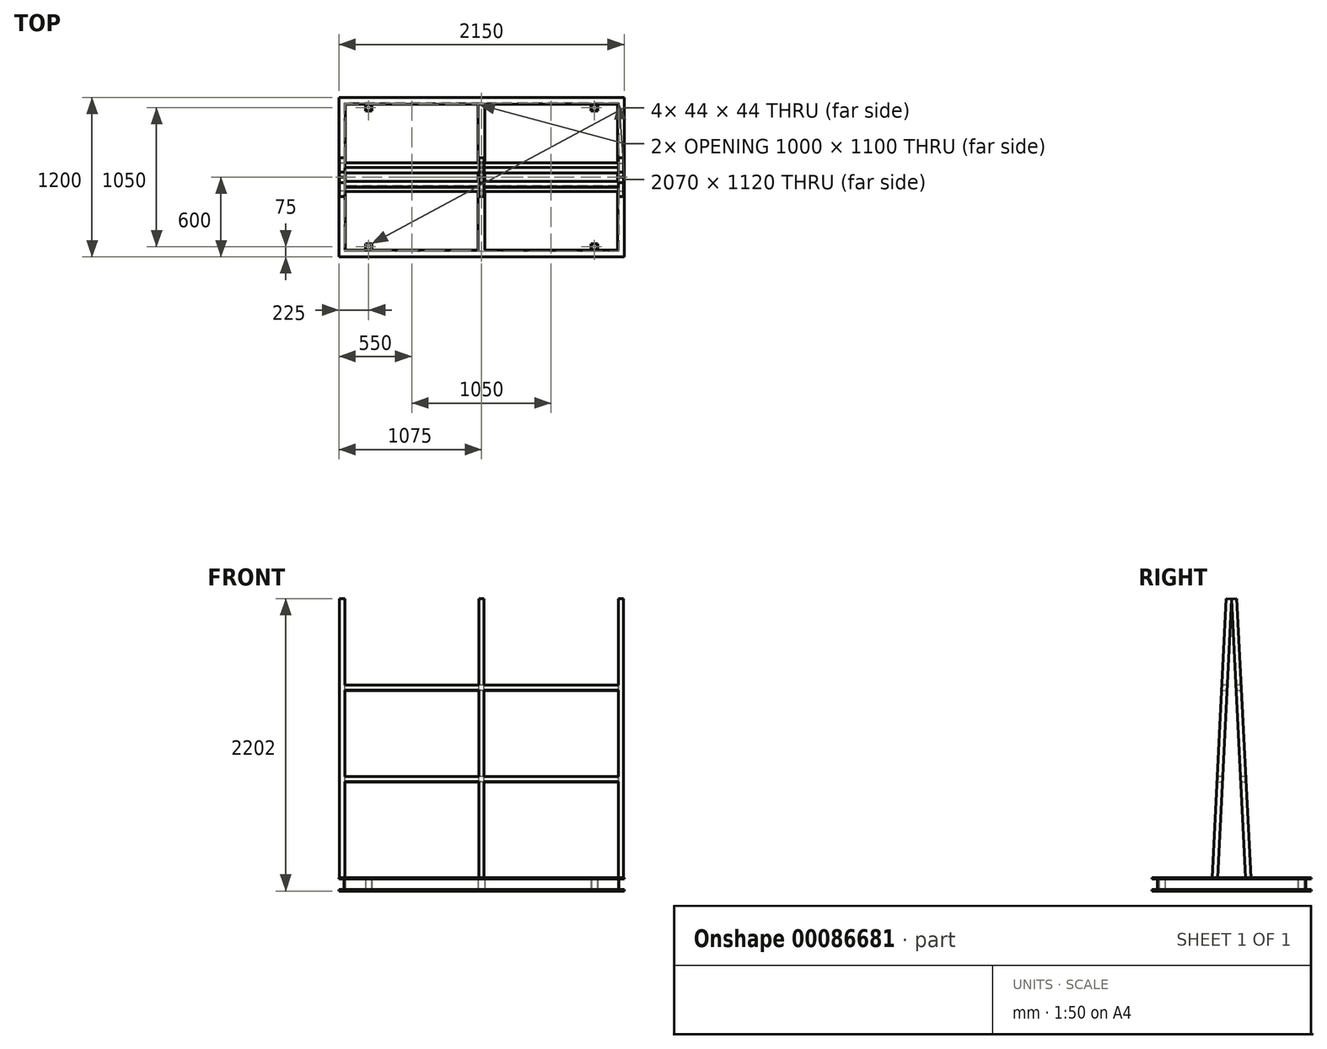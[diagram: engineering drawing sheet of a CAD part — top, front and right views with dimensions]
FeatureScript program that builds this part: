
annotation { "Feature Type Name" : "Feature", "Feature Type Description" : "" }
export const myFeature = defineFeature(function(context is Context, id is Id, definition is map)
    precondition{}
    {
        {
            var Q0;
            Q0=qCreatedBy(makeId("Top.planeOp"),FACE);
            var sketch = newSketch(context, id + "F0", { "sketchPlane" : qUnion([Q0])});
            skLineSegment(sketch, "E0.rect.bottom", {"start": v(1075, 600) * mm, "end": v(-1075, 600) * mm});
            skLineSegment(sketch, "E0.rect.top", {"start": v(1075, -600) * mm, "end": v(-1075, -600) * mm});
            skLineSegment(sketch, "E0.rect.left", {"start": v(1075, 600) * mm, "end": v(1075, -600) * mm});
            skLineSegment(sketch, "E0.rect.right", {"start": v(-1075, 600) * mm, "end": v(-1075, -600) * mm});
            skPoint(sketch, "E0.rect.middle", {"position": v(0, 0) * mm});
            skLineSegment(sketch, "E1.rect.bottom", {"start": v(1025, 550) * mm, "end": v(25, 550) * mm});
            skLineSegment(sketch, "E1.rect.top", {"start": v(1025, -550) * mm, "end": v(25, -550) * mm});
            skLineSegment(sketch, "E1.rect.left", {"start": v(1025, 550) * mm, "end": v(1025, -550) * mm});
            skLineSegment(sketch, "E1.rect.right", {"start": v(-1025, 550) * mm, "end": v(-1025, -550) * mm});
            skLineSegment(sketch, "E2.rect.left", {"start": v(25, 550) * mm, "end": v(25, -550) * mm});
            skLineSegment(sketch, "E2.rect.right", {"start": v(-25, 550) * mm, "end": v(-25, -550) * mm});
            skLineSegment(sketch, "E3.trimOffspring", {"start": v(-25, 550) * mm, "end": v(-1025, 550) * mm});
            skLineSegment(sketch, "E4.trimOffspring", {"start": v(-25, -550) * mm, "end": v(-1025, -550) * mm});
            skSolve(sketch);
        }
        {
            var Q0;
            Q0=makeQuery(id+"F0.imprint","IMPRINT",FACE,{"disambiguationData":[TD([[makeQuery(id+"F0.imprint","IMPRINT",EDGE,{"derivedFrom":sQuery(id+"F0.wireOp",EDGE,"E0.rect.bottom")}),1.0]])]});
            extrude(context, id + "F1", {"entities" : qUnion([Q0]), "depth" : 100 * mm});
        }
        {
            var Q0;
            Q0=makeQuery(id+"F1.opExtrude","SWEPT_FACE",FACE,{"disambiguationData":[OSD([sQuery(id+"F0.wireOp",EDGE,"E0.rect.right")])]});
            var sketch = newSketch(context, id + "F2", { "sketchPlane" : qUnion([Q0])});
            skLineSegment(sketch, "E5.bottom", {"start": v(-600, 90) * mm, "end": v(-560, 90) * mm});
            skLineSegment(sketch, "E5.top", {"start": v(-600, 10) * mm, "end": v(-560, 10) * mm});
            skLineSegment(sketch, "E5.left", {"start": v(-600, 90) * mm, "end": v(-600, 10) * mm});
            skLineSegment(sketch, "E5.right", {"start": v(-560, 90) * mm, "end": v(-560, 10) * mm});
            skLineSegment(sketch, "E6.bottom", {"start": v(600, 90) * mm, "end": v(560, 90) * mm});
            skLineSegment(sketch, "E6.top", {"start": v(600, 10) * mm, "end": v(560, 10) * mm});
            skLineSegment(sketch, "E6.left", {"start": v(600, 90) * mm, "end": v(600, 10) * mm});
            skLineSegment(sketch, "E6.right", {"start": v(560, 90) * mm, "end": v(560, 10) * mm});
            skSolve(sketch);
        }
        {
            var Q0;
            Q0=makeQuery(id+"F2.imprint","IMPRINT",FACE,{"disambiguationData":[TD([[makeQuery(id+"F2.imprint","IMPRINT",EDGE,{"derivedFrom":sQuery(id+"F2.wireOp",EDGE,"E5.bottom")}),-1.0]])]});
            var Q1;
            Q1=makeQuery(id+"F2.imprint","IMPRINT",FACE,{"disambiguationData":[TD([[makeQuery(id+"F2.imprint","IMPRINT",EDGE,{"derivedFrom":sQuery(id+"F2.wireOp",EDGE,"E6.bottom")}),1.0]])]});
            extrude(context, id + "F3", {"entities" : qUnion([Q0, Q1]), "operationType" : NewBodyOperationType.REMOVE, "endBound" : BoundingType.THROUGH_ALL, "oppositeDirection" : true, "depth" : 25 * mm});
        }
        {
            var Q0;
            Q0=makeQuery(id+"F3.boolean.opBoolean","COPY",FACE,{"derivedFrom":makeQuery(id+"F3.opExtrude","SWEPT_FACE",FACE,{"disambiguationData":[OSD([sQuery(id+"F2.wireOp",EDGE,"E6.right")])]})});
            var sketch = newSketch(context, id + "F4", { "sketchPlane" : qUnion([Q0])});
            skLineSegment(sketch, "E7.bottom", {"start": v(1075, 90) * mm, "end": v(1035, 90) * mm});
            skLineSegment(sketch, "E7.top", {"start": v(1075, 10) * mm, "end": v(1035, 10) * mm});
            skLineSegment(sketch, "E7.left", {"start": v(1075, 90) * mm, "end": v(1075, 10) * mm});
            skLineSegment(sketch, "E7.right", {"start": v(1035, 90) * mm, "end": v(1035, 10) * mm});
            skLineSegment(sketch, "E8.bottom", {"start": v(-1075, 90) * mm, "end": v(-1035, 90) * mm});
            skLineSegment(sketch, "E8.top", {"start": v(-1075, 10) * mm, "end": v(-1035, 10) * mm});
            skLineSegment(sketch, "E8.left", {"start": v(-1075, 90) * mm, "end": v(-1075, 10) * mm});
            skLineSegment(sketch, "E8.right", {"start": v(-1035, 90) * mm, "end": v(-1035, 10) * mm});
            skSolve(sketch);
        }
        {
            var Q0;
            Q0=makeQuery(id+"F4.imprint","IMPRINT",FACE,{"disambiguationData":[TD([[makeQuery(id+"F4.imprint","IMPRINT",EDGE,{"derivedFrom":sQuery(id+"F4.wireOp",EDGE,"E7.bottom")}),1.0]])]});
            var Q1;
            Q1=makeQuery(id+"F4.imprint","IMPRINT",FACE,{"disambiguationData":[TD([[makeQuery(id+"F4.imprint","IMPRINT",EDGE,{"derivedFrom":sQuery(id+"F4.wireOp",EDGE,"E8.bottom")}),1.0]])]});
            extrude(context, id + "F5", {"entities" : qUnion([Q0, Q1]), "operationType" : NewBodyOperationType.REMOVE, "endBound" : BoundingType.THROUGH_ALL, "oppositeDirection" : true, "depth" : 25 * mm});
        }
        {
            var Q0;
            Q0=qCreatedBy(makeId("Front.planeOp"),FACE);
            var sketch = newSketch(context, id + "F6", { "sketchPlane" : qUnion([Q0])});
            skLineSegment(sketch, "E9.bottom", {"start": v(0, 10) * mm, "end": v(-90, 10) * mm});
            skLineSegment(sketch, "E9.top", {"start": v(0, 90) * mm, "end": v(-90, 90) * mm});
            skLineSegment(sketch, "E9.left", {"start": v(0, 10) * mm, "end": v(0, 90) * mm});
            skLineSegment(sketch, "E9.right", {"start": v(-90, 10) * mm, "end": v(-90, 90) * mm});
            skSolve(sketch);
        }
        {
            var Q0;
            Q0=qSketchRegion(id+"F6",true);
            var Q1;
            Q1=makeQuery(id+"F1.opExtrude","SWEPT_FACE",FACE,{"disambiguationData":[OSD([sQuery(id+"F0.wireOp",EDGE,"E3.trimOffspring")])]});
            var Q2;
            Q2=makeQuery(id+"F1.opExtrude","SWEPT_FACE",FACE,{"disambiguationData":[OSD([sQuery(id+"F0.wireOp",EDGE,"E4.trimOffspring")])]});
            extrude(context, id + "F7", {"entities" : qUnion([Q0]), "operationType" : NewBodyOperationType.REMOVE, "endBound" : BoundingType.UP_TO_SURFACE, "oppositeDirection" : true, "endBoundEntityFace" : qUnion([Q1]), "depth" : 25 * mm, "hasSecondDirection" : true, "secondDirectionBound" : SecondDirectionBoundingType.UP_TO_SURFACE, "secondDirectionOppositeDirection" : false, "secondDirectionBoundEntityFace" : qUnion([Q2]), "secondDirectionDepth" : 25 * mm});
        }
        {
            var Q0;
            Q0=qCreatedBy(makeId("Right.planeOp"),FACE);
            cPlane(context, id + "F8", {"entities" : qUnion([Q0]), "cplaneType" : CPlaneType.OFFSET, "offset" : 525 * mm, "width" : 150 * mm, "height" : 150 * mm});
        }
        {
            var Q0;
            Q0=qCreatedBy(makeId("Right.planeOp"),FACE);
            var sketch = newSketch(context, id + "F9", { "sketchPlane" : qUnion([Q0])});
            skLineSegment(sketch, "E10", {"start": v(144.95, 100) * mm, "end": v(-249.42, 100) * mm});
            skLineSegment(sketch, "E11", {"start": v(0, 0) * mm, "end": v(185.49, 0) * mm});
            skLineSegment(sketch, "E12", {"start": v(104.9, 100) * mm, "end": v(-0.05, 2200) * mm});
            skLineSegment(sketch, "E13", {"start": v(-105, 100) * mm, "end": v(0, 2200) * mm});
            skLineSegment(sketch, "E14.0", {"start": v(144.95, 100) * mm, "end": v(39.9, 2202) * mm});
            skLineSegment(sketch, "E15.0", {"start": v(-145.05, 100) * mm, "end": v(-39.95, 2202) * mm});
            skLineSegment(sketch, "E16", {"start": v(-39.95, 2202) * mm, "end": v(0, 2200) * mm});
            skLineSegment(sketch, "E17", {"start": v(-0.05, 2200) * mm, "end": v(39.9, 2202) * mm});
            skLineSegment(sketch, "E18", {"start": v(0, 0) * mm, "end": v(0, 2304.84) * mm});
            skSolve(sketch);
        }
        {
            var Q0;
            {var subQ7=sQuery(id+"F9.wireOp",EDGE,"E15.0");Q0=makeQuery(id+"F9.imprint","IMPRINT",FACE,{"disambiguationData":[TD([[makeQuery(id+"F9.imprint","IMPRINT",EDGE,{"derivedFrom":subQ7}),-1.0]])]});}
            var Q1;
            {var subQ1=sQuery(id+"F9.wireOp",EDGE,"E14.0");Q1=makeQuery(id+"F9.imprint","IMPRINT",FACE,{"disambiguationData":[TD([[makeQuery(id+"F9.imprint","IMPRINT",EDGE,{"derivedFrom":subQ1}),1.0]])]});}
            extrude(context, id + "F10", {"entities" : qUnion([Q0, Q1]), "endBound" : BoundingType.SYMMETRIC, "depth" : 40 * mm});
        }
        {
            var Q0;
            Q0=makeQuery(id+"F10.opExtrude","SWEPT_BODY",BODY,{"disambiguationData":[OSD([sQuery(id+"F9.wireOp",EDGE,"E10"),sQuery(id+"F9.wireOp",EDGE,"E12"),sQuery(id+"F9.wireOp",EDGE,"E14.0"),sQuery(id+"F9.wireOp",EDGE,"E17"),sQuery(id+"F9.wireOp",EDGE,"E18")])]});
            var Q1;
            Q1=makeQuery(id+"F10.opExtrude","SWEPT_BODY",BODY,{"disambiguationData":[OSD([sQuery(id+"F9.wireOp",EDGE,"E10"),sQuery(id+"F9.wireOp",EDGE,"E12"),sQuery(id+"F9.wireOp",EDGE,"E13"),sQuery(id+"F9.wireOp",EDGE,"E15.0"),sQuery(id+"F9.wireOp",EDGE,"E16"),sQuery(id+"F9.wireOp",EDGE,"E17")])]});
            var Q2;
            Q2=qCreatedBy(id+"F8.planeOp",FACE);
            mirror(context, id + "F11", {"operationType" : NewBodyOperationType.ADD, "entities" : qUnion([Q0, Q1]), "mirrorPlane" : qUnion([Q2])});
        }
        {
            var Q0;
            Q0=makeQuery(id+"F1.opExtrude","SWEPT_BODY",BODY,{"disambiguationData":[OSD([sQuery(id+"F0.wireOp",EDGE,"E0.rect.bottom"),sQuery(id+"F0.wireOp",EDGE,"E0.rect.top"),sQuery(id+"F0.wireOp",EDGE,"E0.rect.left"),sQuery(id+"F0.wireOp",EDGE,"E0.rect.right"),sQuery(id+"F0.wireOp",EDGE,"E1.rect.bottom"),sQuery(id+"F0.wireOp",EDGE,"E1.rect.top"),sQuery(id+"F0.wireOp",EDGE,"E1.rect.left"),sQuery(id+"F0.wireOp",EDGE,"E1.rect.right"),sQuery(id+"F0.wireOp",EDGE,"E2.rect.left"),sQuery(id+"F0.wireOp",EDGE,"E2.rect.right"),sQuery(id+"F0.wireOp",EDGE,"E3.trimOffspring"),sQuery(id+"F0.wireOp",EDGE,"E4.trimOffspring")])]});
            var Q1;
            Q1=makeQuery(id+"F1.opExtrude","SWEPT_BODY",BODY,{"disambiguationData":[OSD([sQuery(id+"F0.wireOp",EDGE,"E0.rect.bottom"),sQuery(id+"F0.wireOp",EDGE,"E0.rect.top"),sQuery(id+"F0.wireOp",EDGE,"E0.rect.left"),sQuery(id+"F0.wireOp",EDGE,"E0.rect.right"),sQuery(id+"F0.wireOp",EDGE,"E1.rect.bottom"),sQuery(id+"F0.wireOp",EDGE,"E1.rect.top"),sQuery(id+"F0.wireOp",EDGE,"E1.rect.left"),sQuery(id+"F0.wireOp",EDGE,"E1.rect.right"),sQuery(id+"F0.wireOp",EDGE,"E2.rect.left"),sQuery(id+"F0.wireOp",EDGE,"E2.rect.right"),sQuery(id+"F0.wireOp",EDGE,"E3.trimOffspring"),sQuery(id+"F0.wireOp",EDGE,"E4.trimOffspring")])]});
            var Q2;
            Q2=qCreatedBy(makeId("Right.planeOp"),FACE);
            mirror(context, id + "F12", {"operationType" : NewBodyOperationType.ADD, "entities" : qUnion([Q0, Q1]), "mirrorPlane" : qUnion([Q2])});
        }
        {
            var Q0;
            Q0=makeQuery(id+"F12.opPattern","COPY",FACE,{"derivedFrom":makeQuery(id+"F11.opPattern","COPY",FACE,{"derivedFrom":makeQuery(id+"F10.opExtrude","CAP_FACE",FACE,{"disambiguationData":[OSD([sQuery(id+"F9.wireOp",EDGE,"E10"),sQuery(id+"F9.wireOp",EDGE,"E12"),sQuery(id+"F9.wireOp",EDGE,"E13"),sQuery(id+"F9.wireOp",EDGE,"E15.0"),sQuery(id+"F9.wireOp",EDGE,"E16"),sQuery(id+"F9.wireOp",EDGE,"E17")])],"isStart":false}),"instanceName":"1"}),"instanceName":"1"});
            var sketch = newSketch(context, id + "F13", { "sketchPlane" : qUnion([Q0])});
            skLineSegment(sketch, "E19", {"start": v(-72.4, 1552.8) * mm, "end": v(-32.46, 1550.81) * mm});
            skLineSegment(sketch, "E20", {"start": v(-32.46, 1550.81) * mm, "end": v(-34.46, 1510.86) * mm});
            skLineSegment(sketch, "E21", {"start": v(-34.46, 1510.86) * mm, "end": v(-74.4, 1512.86) * mm});
            skLineSegment(sketch, "E22", {"start": v(-74.4, 1512.86) * mm, "end": v(-72.4, 1552.8) * mm});
            skLineSegment(sketch, "E23", {"start": v(-106.87, 863.67) * mm, "end": v(-66.92, 861.67) * mm});
            skLineSegment(sketch, "E24", {"start": v(-66.92, 861.67) * mm, "end": v(-68.91, 821.72) * mm});
            skLineSegment(sketch, "E25", {"start": v(-68.91, 821.72) * mm, "end": v(-108.86, 823.72) * mm});
            skLineSegment(sketch, "E26", {"start": v(-108.86, 823.72) * mm, "end": v(-106.87, 863.67) * mm});
            skSolve(sketch);
        }
        {
            var Q0;
            Q0=makeQuery(id+"F13.imprint","IMPRINT",FACE,{"disambiguationData":[TD([[makeQuery(id+"F13.imprint","IMPRINT",EDGE,{"derivedFrom":sQuery(id+"F13.wireOp",EDGE,"E19")}),-1.0]])]});
            var Q1;
            Q1=makeQuery(id+"F13.imprint","IMPRINT",FACE,{"disambiguationData":[TD([[makeQuery(id+"F13.imprint","IMPRINT",EDGE,{"derivedFrom":sQuery(id+"F13.wireOp",EDGE,"E23")}),-1.0]])]});
            var Q2;
            Q2=makeQuery(id+"F11.opPattern","COPY",FACE,{"derivedFrom":makeQuery(id+"F10.opExtrude","CAP_FACE",FACE,{"disambiguationData":[OSD([sQuery(id+"F9.wireOp",EDGE,"E10"),sQuery(id+"F9.wireOp",EDGE,"E12"),sQuery(id+"F9.wireOp",EDGE,"E13"),sQuery(id+"F9.wireOp",EDGE,"E15.0"),sQuery(id+"F9.wireOp",EDGE,"E16"),sQuery(id+"F9.wireOp",EDGE,"E17")])],"isStart":false}),"instanceName":"1"});
            extrude(context, id + "F14", {"entities" : qUnion([Q0, Q1]), "endBound" : BoundingType.UP_TO_SURFACE, "endBoundEntityFace" : qUnion([Q2]), "depth" : 25 * mm});
        }
        {
            var Q0;
            Q0=makeQuery(id+"F14.opExtrude","SWEPT_BODY",BODY,{"disambiguationData":[OSD([sQuery(id+"F13.wireOp",EDGE,"E19"),sQuery(id+"F13.wireOp",EDGE,"E20"),sQuery(id+"F13.wireOp",EDGE,"E21"),sQuery(id+"F13.wireOp",EDGE,"E22")])]});
            var Q1;
            Q1=makeQuery(id+"F14.opExtrude","SWEPT_BODY",BODY,{"disambiguationData":[OSD([sQuery(id+"F13.wireOp",EDGE,"E23"),sQuery(id+"F13.wireOp",EDGE,"E24"),sQuery(id+"F13.wireOp",EDGE,"E25"),sQuery(id+"F13.wireOp",EDGE,"E26")])]});
            var Q2;
            Q2=qCreatedBy(makeId("Front.planeOp"),FACE);
            mirror(context, id + "F15", {"operationType" : NewBodyOperationType.ADD, "entities" : qUnion([Q0, Q1]), "mirrorPlane" : qUnion([Q2])});
        }
        {
            var Q0;
            Q0=qCreatedBy(makeId("Top.planeOp"),FACE);
            var sketch = newSketch(context, id + "F16", { "sketchPlane" : qUnion([Q0])});
            skLineSegment(sketch, "E27.bottom", {"start": v(-875, -550) * mm, "end": v(-825, -550) * mm});
            skLineSegment(sketch, "E27.top", {"start": v(-875, -500) * mm, "end": v(-825, -500) * mm});
            skLineSegment(sketch, "E27.left", {"start": v(-875, -550) * mm, "end": v(-875, -500) * mm});
            skLineSegment(sketch, "E27.right", {"start": v(-825, -550) * mm, "end": v(-825, -500) * mm});
            skLineSegment(sketch, "E28.bottom", {"start": v(-875, 550) * mm, "end": v(-825, 550) * mm});
            skLineSegment(sketch, "E28.top", {"start": v(-875, 500) * mm, "end": v(-825, 500) * mm});
            skLineSegment(sketch, "E28.left", {"start": v(-875, 550) * mm, "end": v(-875, 500) * mm});
            skLineSegment(sketch, "E28.right", {"start": v(-825, 550) * mm, "end": v(-825, 500) * mm});
            skLineSegment(sketch, "E29.bottom", {"start": v(875, 550) * mm, "end": v(825, 550) * mm});
            skLineSegment(sketch, "E29.top", {"start": v(825, 500) * mm, "end": v(875, 500) * mm});
            skLineSegment(sketch, "E29.left", {"start": v(825, 550) * mm, "end": v(825, 500) * mm});
            skLineSegment(sketch, "E29.right", {"start": v(875, 550) * mm, "end": v(875, 500) * mm});
            skLineSegment(sketch, "E30.bottom", {"start": v(825, -550) * mm, "end": v(875, -550) * mm});
            skLineSegment(sketch, "E30.top", {"start": v(825, -500) * mm, "end": v(875, -500) * mm});
            skLineSegment(sketch, "E30.left", {"start": v(825, -550) * mm, "end": v(825, -500) * mm});
            skLineSegment(sketch, "E30.right", {"start": v(875, -550) * mm, "end": v(875, -500) * mm});
            skLineSegment(sketch, "E31.bottom", {"start": v(-872, 547) * mm, "end": v(-828, 547) * mm});
            skLineSegment(sketch, "E31.top", {"start": v(-872, 503) * mm, "end": v(-828, 503) * mm});
            skLineSegment(sketch, "E31.left", {"start": v(-872, 547) * mm, "end": v(-872, 503) * mm});
            skLineSegment(sketch, "E31.right", {"start": v(-828, 547) * mm, "end": v(-828, 503) * mm});
            skLineSegment(sketch, "E32.bottom", {"start": v(828, 547) * mm, "end": v(872, 547) * mm});
            skLineSegment(sketch, "E32.top", {"start": v(828, 503) * mm, "end": v(872, 503) * mm});
            skLineSegment(sketch, "E32.left", {"start": v(828, 547) * mm, "end": v(828, 503) * mm});
            skLineSegment(sketch, "E32.right", {"start": v(872, 547) * mm, "end": v(872, 503) * mm});
            skLineSegment(sketch, "E33.bottom", {"start": v(-872, -503) * mm, "end": v(-828, -503) * mm});
            skLineSegment(sketch, "E33.top", {"start": v(-872, -547) * mm, "end": v(-828, -547) * mm});
            skLineSegment(sketch, "E33.left", {"start": v(-872, -503) * mm, "end": v(-872, -547) * mm});
            skLineSegment(sketch, "E33.right", {"start": v(-828, -503) * mm, "end": v(-828, -547) * mm});
            skLineSegment(sketch, "E34.bottom", {"start": v(828, -503) * mm, "end": v(872, -503) * mm});
            skLineSegment(sketch, "E34.top", {"start": v(828, -547) * mm, "end": v(872, -547) * mm});
            skLineSegment(sketch, "E34.left", {"start": v(828, -503) * mm, "end": v(828, -547) * mm});
            skLineSegment(sketch, "E34.right", {"start": v(872, -503) * mm, "end": v(872, -547) * mm});
            skSolve(sketch);
        }
        {
            var Q0;
            Q0=makeQuery(id+"F16.imprint","IMPRINT",FACE,{"disambiguationData":[TD([[makeQuery(id+"F16.imprint","IMPRINT",EDGE,{"derivedFrom":sQuery(id+"F16.wireOp",EDGE,"E28.bottom")}),-1.0]])]});
            var Q1;
            Q1=makeQuery(id+"F16.imprint","IMPRINT",FACE,{"disambiguationData":[TD([[makeQuery(id+"F16.imprint","IMPRINT",EDGE,{"derivedFrom":sQuery(id+"F16.wireOp",EDGE,"E29.bottom")}),1.0]])]});
            var Q2;
            Q2=makeQuery(id+"F16.imprint","IMPRINT",FACE,{"disambiguationData":[TD([[makeQuery(id+"F16.imprint","IMPRINT",EDGE,{"derivedFrom":sQuery(id+"F16.wireOp",EDGE,"E30.bottom")}),1.0]])]});
            var Q3;
            Q3=makeQuery(id+"F16.imprint","IMPRINT",FACE,{"disambiguationData":[TD([[makeQuery(id+"F16.imprint","IMPRINT",EDGE,{"derivedFrom":sQuery(id+"F16.wireOp",EDGE,"E27.bottom")}),1.0]])]});
            extrude(context, id + "F17", {"entities" : qUnion([Q0, Q1, Q2, Q3]), "operationType" : NewBodyOperationType.ADD, "depth" : 100 * mm});
        }
    });
